# Revit family: AB-QM 4.0_CO6 Flexo_DN15_AME 110 NL(X)_RFA_1
name_source: partatom
category: Pipe Accessories
units: mm (PartAtom-declared; Revit-internal decimal feet)

## family parameters
Always vertical = Yes
Cut with Voids When Loaded = No
OmniClass Number = 23.65.55.14
OmniClass Title = Valves for Liquid Services
Part Type = Valve - Normal
Round Connector Dimension = Use Diameter
Shared = No
Work Plane-Based = No

## types (4) — shared parameters
Actuator Type = AME 110 NL(X)_RFA : AME 110 NL_1.5m_082H8110
Actuator Type 2 = Actuator CO6_RFA : Actuator ChangeOver6_24V_1.5m_003Z3152
Body Material = Danfoss Brass
CO6 Type = ChangeOver6_DN15-DN20_Actuator_RFA : ChangeOver6_DN15_003Z3150
D = 15 mm  [stored 0.0492126 ft]
Description = Motorized 6-way Ball Valve with Pressure Independent Control Valve
IfcExportAs = IfcValveType
IfcExportType = AB-QM 4.0 CO6 Flexo
Kvs = 2.4 m³/h
Kvs one port = 3.4 m³/h
LOD 200 = No
LOD 350 = Yes
Manufacturer = Danfoss
Max Medium Temperature = 90 °C
Min Medium Temperature = 2 °C
Nominal Pressure = PN 16
Nut = 27 mm  [stored 0.0885827 ft]
Pipe Material = Danfoss Stainless Steel
Power 1 = 1 VA
Power 2 = 3 VA
Setting Range = 10-100%
Stroke = 4 mm
URL = https://store.danfoss.com
Valve Body Material = Danfoss Brass (DZR)
Voltage = 24 V
W1 = 36.74 mm  [stored 0.120538 ft]

## per-type parameters (varying)
| type | AB-QM 4.0 Size | CO6 Differential Pressure | Connection | LL | LR | Max Differential Pressure | Model | Model Type | Nominal Flow | Nominal Flow (Text) | R1 | Weight | tailpiece nut |
| AB-QM 4.0_CO6 Flexo_DN15_Tailpiece_003Z1561 | AB-QM 4.0_DN15-DN32_External_TP_AME 110 NL(X)_120 NL_RFA : AB-QM 4.0_DN15_External_TP_003Z8201 | 7.3 kPa | Internal thread | 232.2 mm  [stored 0.761811 ft] | 248.2 mm  [stored 0.814304 ft] | 30 kPa | 003Z1561 | AB-QM 4.0_CO6 Flexo_DN15_Tailpiece | 0.7 m³/h | 700 l/h | 17 mm  [stored 0.0557743 ft] | 3.70 kg | Yes |
| AB-QM 4.0_CO6 Flexo_DN15LF_Tailpiece_003Z1560 | AB-QM 4.0_DN15-DN32_External_TP_AME 110 NL(X)_120 NL_RFA : AB-QM 4.0_DN15LF_External_TP_003Z8200 | 0.7 kPa | Internal thread | 232.2 mm  [stored 0.761811 ft] | 248.2 mm  [stored 0.814304 ft] | 20 kPa | 003Z1560 | AB-QM 4.0_CO6 Flexo_DN15LF_Tailpiece | 0.2 m³/h | 200 l/h | 17 mm  [stored 0.0557743 ft] | 3.70 kg | Yes |
| AB-QM 4.0_CO6 Flexo_DN15_Straight pipe_003Z1581 | AB-QM 4.0_DN15-DN32_External_TP_AME 110 NL(X)_120 NL_RFA : AB-QM 4.0_DN15_External_TP_003Z8201 | 7.3 kPa | Straight pipe 18mm | 215.68 mm  [stored 0.707612 ft] | 231.86 mm  [stored 0.760696 ft] | 30 kPa | 003Z1581 | AB-QM 4.0_CO6 Flexo_DN15_Straight pipe | 0.7 m³/h | 700 l/h | 9 mm  [stored 0.0295276 ft] | 3.30 kg | No |
| AB-QM 4.0_CO6 Flexo_DN15LF_Straight pipe_003Z1580 | AB-QM 4.0_DN15-DN32_External_TP_AME 110 NL(X)_120 NL_RFA : AB-QM 4.0_DN15LF_External_TP_003Z8200 | 0.7 kPa | Straight pipe 18mm | 215.68 mm  [stored 0.707612 ft] | 231.86 mm  [stored 0.760696 ft] | 20 kPa | 003Z1580 | AB-QM 4.0_CO6 Flexo_DN15LF_Straight pipe | 0.2 m³/h | 200 l/h | 9 mm  [stored 0.0295276 ft] | 3.30 kg | No |

note: [stored X ft] marks values corroborated as IEEE doubles in the binary element streams (Revit-internal decimal feet)

## geometry (parser evidence)
native form markers: Blend x4, Sweep x21
no freeform markers — native parametric forms only
